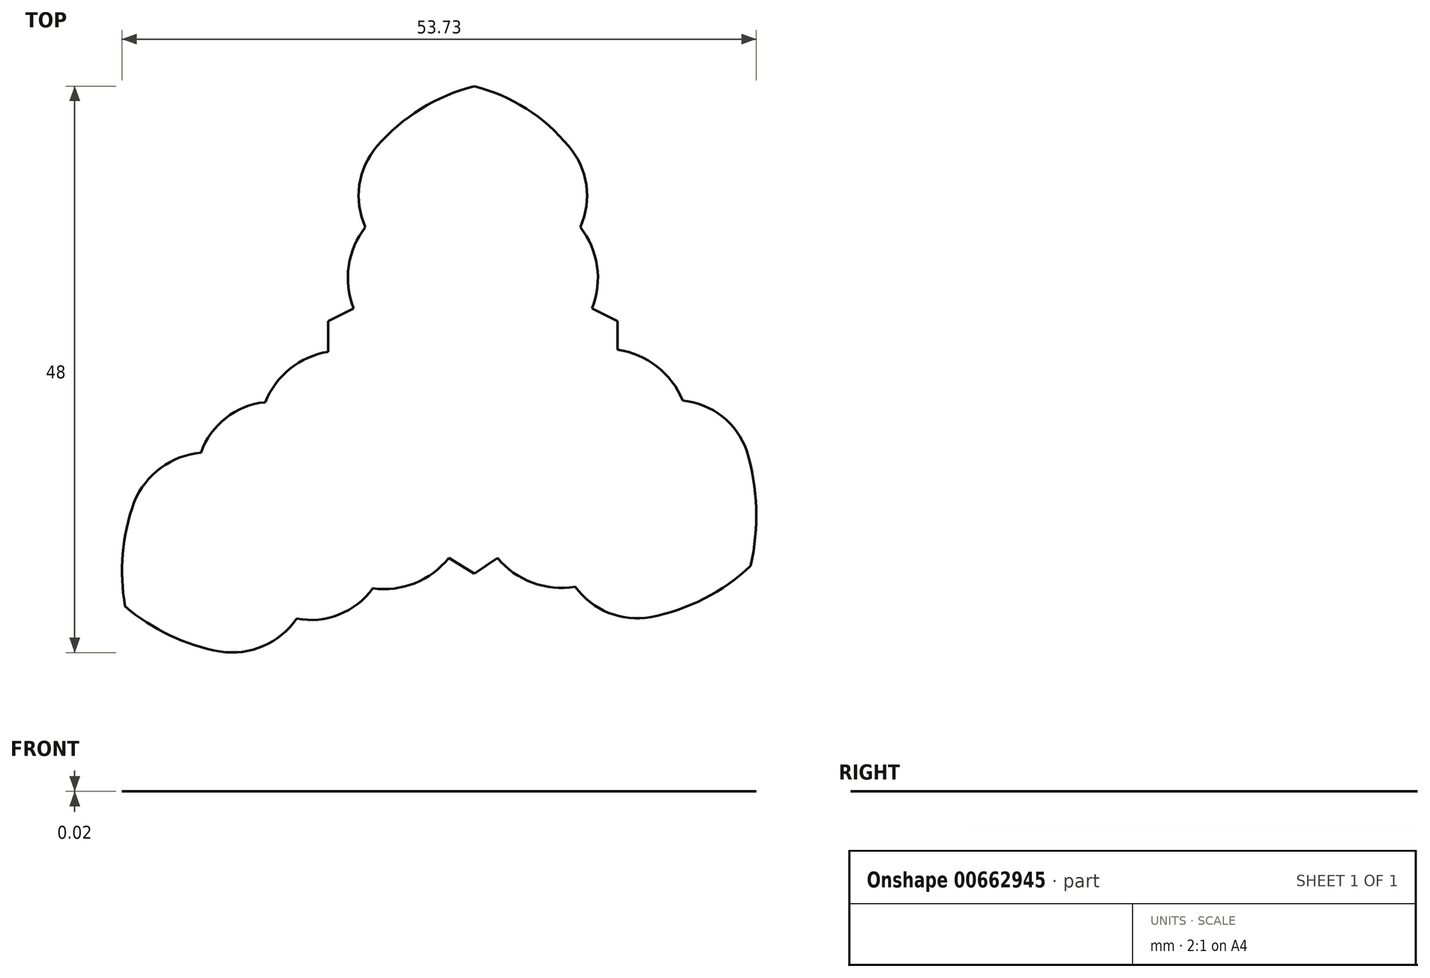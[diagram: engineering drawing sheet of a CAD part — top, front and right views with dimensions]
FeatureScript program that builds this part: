
annotation { "Feature Type Name" : "Feature", "Feature Type Description" : "" }
export const myFeature = defineFeature(function(context is Context, id is Id, definition is map)
    precondition{}
    {
        {
            var Q0;
            Q0=qCreatedBy(makeId("Top.planeOp"),FACE);
            var sketch = newSketch(context, id + "F0", { "sketchPlane" : qUnion([Q0])});
            skPoint(sketch, "E0.center", {"position": v(0, 0) * mm});
            skArc(sketch, "E1", {"start": v(-8.23, 21.98) * mm, "mid": v(-9.72, 18.7) * mm, "end": v(-9.2, 15.13) * mm});
            skArc(sketch, "E2", {"start": v(-9.2, 15.13) * mm, "mid": v(-10.62, 11.82) * mm, "end": v(-10.2, 8.25) * mm});
            skLineSegment(sketch, "E3", {"start": v(-10.2, 8.25) * mm, "end": v(-12.37, 7.15) * mm});
            skLineSegment(sketch, "E4", {"start": v(-12.37, 7.15) * mm, "end": v(-12.37, 4.64) * mm});
            skLineSegment(sketch, "E5.MirrorCS", {"start": v(12.16, 7.15) * mm, "end": v(12.16, 4.64) * mm});
            skLineSegment(sketch, "E6.MirrorCS", {"start": v(10, 8.25) * mm, "end": v(12.16, 7.15) * mm});
            skArc(sketch, "E7.MirrorCS", {"start": v(9, 15.13) * mm, "mid": v(10.4, 11.82) * mm, "end": v(10, 8.25) * mm});
            skArc(sketch, "E8.MirrorCS", {"start": v(8.01, 21.98) * mm, "mid": v(9.5, 18.7) * mm, "end": v(9, 15.13) * mm});
            skArc(sketch, "E9", {"start": v(23.1, -3.85) * mm, "mid": v(21, -0.92) * mm, "end": v(17.66, 0.43) * mm});
            skArc(sketch, "E10", {"start": v(17.66, 0.43) * mm, "mid": v(15.48, 3.32) * mm, "end": v(12.16, 4.74) * mm});
            skArc(sketch, "E11.MirrorCS", {"start": v(8.56, -15.34) * mm, "mid": v(4.94, -15) * mm, "end": v(1.97, -12.9) * mm});
            skArc(sketch, "E12.MirrorCS", {"start": v(14.98, -17.91) * mm, "mid": v(11.4, -17.56) * mm, "end": v(8.56, -15.34) * mm});
            skLineSegment(sketch, "E13", {"start": v(1.97, -12.9) * mm, "end": v(0, -14.26) * mm});
            skLineSegment(sketch, "E14", {"start": v(0, -14.26) * mm, "end": v(-2.14, -12.9) * mm});
            skArc(sketch, "E15", {"start": v(-21.5, -20.86) * mm, "mid": v(-17.86, -20.37) * mm, "end": v(-15.02, -18.05) * mm});
            skArc(sketch, "E16", {"start": v(-15.02, -18.05) * mm, "mid": v(-11.43, -17.7) * mm, "end": v(-8.6, -15.48) * mm});
            skArc(sketch, "E17", {"start": v(-8.6, -15.48) * mm, "mid": v(-5.03, -15.05) * mm, "end": v(-2.14, -12.9) * mm});
            skArc(sketch, "E18.MirrorCS", {"start": v(-17.7, 0.28) * mm, "mid": v(-15.6, 3.12) * mm, "end": v(-12.37, 4.57) * mm});
            skArc(sketch, "E19.MirrorCS", {"start": v(-23.14, -4) * mm, "mid": v(-21.05, -1.06) * mm, "end": v(-17.7, 0.28) * mm});
            skArc(sketch, "E20.MirrorCS", {"start": v(-28.8, -8.2) * mm, "mid": v(-26.56, -5.3) * mm, "end": v(-23.14, -4) * mm});
            skLineSegment(sketch, "E21", {"start": v(-12.37, 4.64) * mm, "end": v(-12.37, 4.57) * mm});
            skArc(sketch, "E22", {"start": v(-28.8, -8.2) * mm, "mid": v(-29.77, -12.56) * mm, "end": v(-29.56, -17.02) * mm});
            skArc(sketch, "E23", {"start": v(-29.56, -17.02) * mm, "mid": v(-25.78, -19.47) * mm, "end": v(-21.5, -20.86) * mm});
            skArc(sketch, "E24", {"start": v(0, 27.07) * mm, "mid": v(-4.5, 25.16) * mm, "end": v(-8.23, 21.98) * mm});
            skArc(sketch, "E25", {"start": v(8.01, 21.98) * mm, "mid": v(4.42, 25.17) * mm, "end": v(0, 27.07) * mm});
            skArc(sketch, "E26", {"start": v(23.42, -13.56) * mm, "mid": v(23.89, -8.68) * mm, "end": v(23.1, -3.85) * mm});
            skArc(sketch, "E27", {"start": v(14.98, -17.91) * mm, "mid": v(19.52, -16.35) * mm, "end": v(23.42, -13.56) * mm});
            skSolve(sketch);
        }
        {
            var Q0;
            Q0=makeQuery(id+"F0.imprint","IMPRINT",FACE,{"disambiguationData":[TD([[makeQuery(id+"F0.imprint","IMPRINT",EDGE,{"derivedFrom":sQuery(id+"F0.wireOp",EDGE,"E1")}),1.0]])]});
            extrude(context, id + "F1", {"entities" : qUnion([Q0]), "depth" : 7 / 406.4 * mm, "offsetDistance" : 25.4 * mm});
        }
    });
